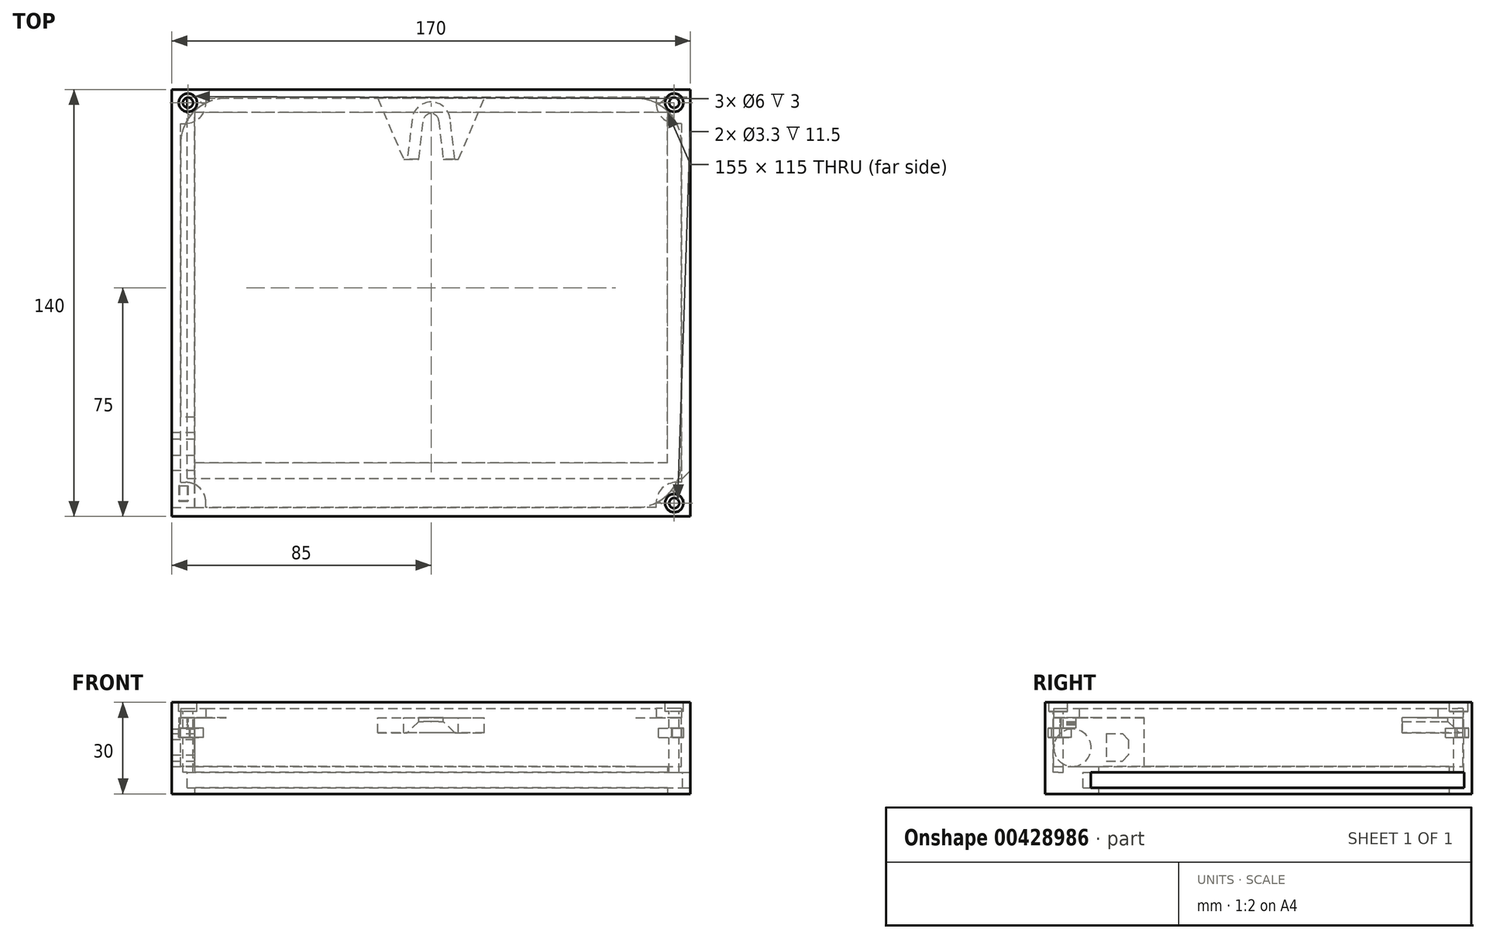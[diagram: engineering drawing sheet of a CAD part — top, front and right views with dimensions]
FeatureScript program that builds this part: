
annotation { "Feature Type Name" : "Feature", "Feature Type Description" : "" }
export const myFeature = defineFeature(function(context is Context, id is Id, definition is map)
    precondition{}
    {
        {
            var Q0;
            Q0=qCreatedBy(makeId("Top.planeOp"),FACE);
            var sketch = newSketch(context, id + "F0", { "sketchPlane" : qUnion([Q0])});
            skLineSegment(sketch, "E0.bottom", {"start": v(0, 0) * mm, "end": v(170, 0) * mm});
            skLineSegment(sketch, "E0.top", {"start": v(0, 140) * mm, "end": v(170, 140) * mm});
            skLineSegment(sketch, "E0.left", {"start": v(0, 0) * mm, "end": v(0, 140) * mm});
            skLineSegment(sketch, "E0.right", {"start": v(170, 0) * mm, "end": v(170, 140) * mm});
            skLineSegment(sketch, "E1.bottom", {"start": v(7.5, 132.5) * mm, "end": v(162.5, 132.5) * mm});
            skLineSegment(sketch, "E1.top", {"start": v(7.5, 17.5) * mm, "end": v(162.5, 17.5) * mm});
            skLineSegment(sketch, "E1.left", {"start": v(7.5, 132.5) * mm, "end": v(7.5, 17.5) * mm});
            skLineSegment(sketch, "E1.right", {"start": v(162.5, 132.5) * mm, "end": v(162.5, 17.5) * mm});
            skSolve(sketch);
        }
        {
            var Q0;
            Q0 = qSketchRegion(id + "F0", true);
            extrude(context, id + "F1", {"entities" : qUnion([Q0]), "depth" : 25 * mm});
        }
        {
            var Q0;
            Q0=makeQuery(id+"F1.opExtrude","SWEPT_FACE",FACE,{"disambiguationData":[OSD([sQuery(id+"F0.wireOp",EDGE,"E0.right")])]});
            var sketch = newSketch(context, id + "F2", { "sketchPlane" : qUnion([Q0])});
            skLineSegment(sketch, "E2.0.0", {"start": v(17.5, 0) * mm, "end": v(132.5, 0) * mm, "construction": true});
            skLineSegment(sketch, "E2.0.1", {"start": v(132.5, 0) * mm, "end": v(132.5, 25) * mm, "construction": true});
            skLineSegment(sketch, "E2.0.2", {"start": v(132.5, 25) * mm, "end": v(17.5, 25) * mm, "construction": true});
            skLineSegment(sketch, "E2.0.3", {"start": v(17.5, 25) * mm, "end": v(17.5, 0) * mm, "construction": true});
            skLineSegment(sketch, "E3.0.3", {"start": v(132.5, 25) * mm, "end": v(132.5, 0) * mm, "construction": true});
            skLineSegment(sketch, "E4.bottom", {"start": v(12.5, 2) * mm, "end": v(137.5, 2) * mm});
            skLineSegment(sketch, "E4.top", {"start": v(12.5, 7) * mm, "end": v(137.5, 7) * mm});
            skLineSegment(sketch, "E4.left", {"start": v(12.5, 2) * mm, "end": v(12.5, 7) * mm});
            skLineSegment(sketch, "E4.right", {"start": v(137.5, 2) * mm, "end": v(137.5, 7) * mm});
            skSolve(sketch);
        }
        {
            var Q0;
            Q0 = qSketchRegion(id + "F2", true);
            extrude(context, id + "F3", {"entities" : qUnion([Q0]), "operationType" : NewBodyOperationType.REMOVE, "oppositeDirection" : true, "depth" : 165 * mm});
        }
        {
            var Q0;
            Q0=makeQuery(id+"F3.boolean.opBoolean","COPY",FACE,{"derivedFrom":makeQuery(id+"F3.opExtrude","SWEPT_FACE",FACE,{"disambiguationData":[OSD([sQuery(id+"F2.wireOp",EDGE,"E4.top")])]})});
            var sketch = newSketch(context, id + "F4", { "sketchPlane" : qUnion([Q0])});
            skLineSegment(sketch, "E5", {"start": v(167.5, -12.5) * mm, "end": v(170, -15) * mm});
            skLineSegment(sketch, "E6", {"start": v(170, -15) * mm, "end": v(170, -12.5) * mm});
            skLineSegment(sketch, "E7", {"start": v(170, -12.5) * mm, "end": v(167.5, -12.5) * mm});
            skSolve(sketch);
        }
        {
            var Q0;
            Q0=makeQuery(id+"F4.imprint","IMPRINT",FACE,{"disambiguationData":[TD([[makeQuery(id+"F4.imprint","IMPRINT",EDGE,{"derivedFrom":sQuery(id+"F4.wireOp",EDGE,"E5")}),1.0]])]});
            extrude(context, id + "F5", {"entities" : qUnion([Q0]), "operationType" : NewBodyOperationType.ADD, "endBound" : BoundingType.UP_TO_NEXT, "depth" : 25 * mm});
        }
        {
            var Q0;
            Q0=makeQuery(id+"F1.opExtrude","CAP_FACE",FACE,{"disambiguationData":[OSD([sQuery(id+"F0.wireOp",EDGE,"E0.bottom"),sQuery(id+"F0.wireOp",EDGE,"E0.top"),sQuery(id+"F0.wireOp",EDGE,"E0.left"),sQuery(id+"F0.wireOp",EDGE,"E0.right"),sQuery(id+"F0.wireOp",EDGE,"E1.bottom"),sQuery(id+"F0.wireOp",EDGE,"E1.top"),sQuery(id+"F0.wireOp",EDGE,"E1.left"),sQuery(id+"F0.wireOp",EDGE,"E1.right")])],"isStart":false});
            var sketch = newSketch(context, id + "F6", { "sketchPlane" : qUnion([Q0])});
            skLineSegment(sketch, "E8.0", {"start": v(167.12, 137.12) * mm, "end": v(2.88, 137.12) * mm});
            skLineSegment(sketch, "E8.1", {"start": v(167.12, 2.88) * mm, "end": v(167.12, 137.12) * mm});
            skLineSegment(sketch, "E8.2", {"start": v(2.88, 2.88) * mm, "end": v(167.12, 2.88) * mm});
            skLineSegment(sketch, "E8.3", {"start": v(2.88, 137.12) * mm, "end": v(2.88, 2.88) * mm});
            skSolve(sketch);
        }
        {
            var Q0;
            Q0 = qSketchRegion(id + "F6", true);
            extrude(context, id + "F7", {"entities" : qUnion([Q0]), "operationType" : NewBodyOperationType.REMOVE, "oppositeDirection" : true, "depth" : 16 * mm});
        }
        {
            var Q0;
            Q0=makeQuery(id+"F7.boolean.opBoolean","COPY",EDGE,{"derivedFrom":makeQuery(id+"F7.opExtrude","SWEPT_EDGE",EDGE,{"disambiguationData":[OSD([sQuery(id+"F6.wireOp",EDGE,"E8.0"),sQuery(id+"F6.wireOp",EDGE,"E8.3")])]})});
            var Q1;
            Q1=makeQuery(id+"F7.boolean.opBoolean","COPY",EDGE,{"derivedFrom":makeQuery(id+"F7.opExtrude","SWEPT_EDGE",EDGE,{"disambiguationData":[OSD([sQuery(id+"F6.wireOp",EDGE,"E8.0"),sQuery(id+"F6.wireOp",EDGE,"E8.1")])]})});
            var Q2;
            Q2=makeQuery(id+"F7.boolean.opBoolean","COPY",EDGE,{"derivedFrom":makeQuery(id+"F7.opExtrude","SWEPT_EDGE",EDGE,{"disambiguationData":[OSD([sQuery(id+"F6.wireOp",EDGE,"E8.1"),sQuery(id+"F6.wireOp",EDGE,"E8.2")])]})});
            fillet(context, id + "F8", {"entities" : qUnion([Q0, Q1, Q2]), "radius" : 15 * mm, "tangentPropagation" : true, "allowEdgeOverflow" : false});
        }
        {
            var Q0;
            Q0=makeQuery(id+"F7.boolean.opBoolean","COPY",FACE,{"derivedFrom":makeQuery(id+"F7.opExtrude","SWEPT_FACE",FACE,{"disambiguationData":[OSD([sQuery(id+"F6.wireOp",EDGE,"E8.3")])]})});
            var sketch = newSketch(context, id + "F9", { "sketchPlane" : qUnion([Q0])});
            skLineSegment(sketch, "E9.0.0", {"start": v(2.88, 9) * mm, "end": v(122.12, 9) * mm, "construction": true});
            skLineSegment(sketch, "E9.0.1", {"start": v(122.12, 9) * mm, "end": v(122.12, 25) * mm, "construction": true});
            skLineSegment(sketch, "E9.0.2", {"start": v(122.12, 25) * mm, "end": v(2.88, 25) * mm, "construction": true});
            skLineSegment(sketch, "E9.0.3", {"start": v(2.88, 25) * mm, "end": v(2.88, 9) * mm, "construction": true});
            skCircle(sketch, "E10", {"center": v(9, 15.13) * mm, "radius": 6.12 * mm});
            skSolve(sketch);
        }
        {
            var Q0;
            {var subQ0=sQuery(id+"F9.wireOp",EDGE,"E10");var subQ1=sQuery(id+"F6.wireOp",EDGE,"E8.3");var subQ3=makeQuery(id+"F9.imprint","INTERSECT",VERTEX,{"derivedFrom":[makeQuery(id+"F7.boolean.opBoolean","COPY",EDGE,{"derivedFrom":makeQuery(id+"F7.opExtrude","CAP_EDGE",EDGE,{"disambiguationData":[OSD([subQ1])],"isStart":false})}),subQ0]});Q0=makeQuery(id+"F9.imprint","IMPRINT",FACE,{"disambiguationData":[TD([[makeQuery(id+"F9.imprint","IMPRINT",EDGE,{"disambiguationData":[TD([[subQ3,1.0]])],"derivedFrom":subQ0}),1.0]])]});}
            extrude(context, id + "F10", {"entities" : qUnion([Q0]), "operationType" : NewBodyOperationType.REMOVE, "endBound" : BoundingType.THROUGH_ALL, "oppositeDirection" : true, "depth" : 25 * mm});
        }
        {
            var Q0;
            {var subQ0=sQuery(id+"F6.wireOp",EDGE,"E8.3");var subQ1=makeQuery(id+"F7.boolean.opBoolean","COPY",FACE,{"derivedFrom":makeQuery(id+"F7.opExtrude","SWEPT_FACE",FACE,{"disambiguationData":[OSD([subQ0])]})});var subQ2=sQuery(id+"F6.wireOp",EDGE,"E8.2");var subQ3=sQuery(id+"F6.wireOp",EDGE,"E8.0");Q0=makeQuery(id+"F10.boolean.opBoolean","SPLIT",FACE,{"disambiguationData":[TD([makeQuery(id+"F1.opExtrude","CAP_FACE",FACE,{"disambiguationData":[OSD([sQuery(id+"F0.wireOp",EDGE,"E0.bottom"),sQuery(id+"F0.wireOp",EDGE,"E0.top"),sQuery(id+"F0.wireOp",EDGE,"E0.left"),sQuery(id+"F0.wireOp",EDGE,"E0.right"),sQuery(id+"F0.wireOp",EDGE,"E1.bottom"),sQuery(id+"F0.wireOp",EDGE,"E1.top"),sQuery(id+"F0.wireOp",EDGE,"E1.left"),sQuery(id+"F0.wireOp",EDGE,"E1.right")])],"isStart":false}),makeQuery(id+"F7.boolean.opBoolean","COPY",FACE,{"derivedFrom":makeQuery(id+"F7.opExtrude","CAP_FACE",FACE,{"disambiguationData":[OSD([subQ3,sQuery(id+"F6.wireOp",EDGE,"E8.1"),subQ2,subQ0])],"isStart":false})}),makeQuery(id+"F7.boolean.opBoolean","COPY",FACE,{"derivedFrom":makeQuery(id+"F7.opExtrude","SWEPT_FACE",FACE,{"disambiguationData":[OSD([subQ2])]})}),subQ1,makeQuery(id+"F8.opFillet","BLEND_FACE",FACE,{"disambiguationData":[OSD([subQ3,subQ0])]}),makeQuery(id+"F10.opExtrude","SWEPT_FACE",FACE,{"disambiguationData":[OSD([sQuery(id+"F9.wireOp",EDGE,"E10")])]})])],"derivedFrom":subQ1});}
            var sketch = newSketch(context, id + "F11", { "sketchPlane" : qUnion([Q0])});
            skArc(sketch, "E11.0", {"start": v(9, 9) * mm, "mid": v(13.34, 19.46) * mm, "end": v(2.88, 15.13) * mm});
            skArc(sketch, "E12.0", {"start": v(2.88, 15.13) * mm, "mid": v(4.67, 10.8) * mm, "end": v(9, 9) * mm});
            skLineSegment(sketch, "E13.bottom", {"start": v(2.88, 9) * mm, "end": v(17.5, 9) * mm});
            skLineSegment(sketch, "E13.top", {"start": v(2.88, 25) * mm, "end": v(17.5, 25) * mm});
            skLineSegment(sketch, "E13.left", {"start": v(2.88, 9) * mm, "end": v(2.88, 25) * mm});
            skLineSegment(sketch, "E13.right", {"start": v(17.5, 9) * mm, "end": v(17.5, 9) * mm});
            skLineSegment(sketch, "E14.0", {"start": v(17.5, 9) * mm, "end": v(17.5, 7) * mm, "construction": true});
            skLineSegment(sketch, "E15", {"start": v(17.5, 9) * mm, "end": v(17.5, 25) * mm});
            skSolve(sketch);
        }
        {
            var Q0;
            Q0 = qSketchRegion(id + "F11", true);
            var Q1;
            {var subQ0=sQuery(id+"F0.wireOp",EDGE,"E1.left");Q1=makeQuery(id+"F3.boolean.opBoolean","SPLIT",FACE,{"disambiguationData":[TD([makeQuery(id+"F3.opExtrude","SWEPT_FACE",FACE,{"disambiguationData":[OSD([sQuery(id+"F2.wireOp",EDGE,"E4.top")])]})])],"derivedFrom":makeQuery(id+"F1.opExtrude","SWEPT_FACE",FACE,{"disambiguationData":[OSD([subQ0])]})});}
            extrude(context, id + "F12", {"entities" : qUnion([Q0]), "operationType" : NewBodyOperationType.ADD, "endBound" : BoundingType.UP_TO_SURFACE, "endBoundEntityFace" : qUnion([Q1]), "depth" : 7.5 * mm});
        }
        {
            var Q0;
            Q0=makeQuery(id+"F12.opExtrude","CAP_FACE",FACE,{"disambiguationData":[OSD([sQuery(id+"F11.wireOp",EDGE,"E13.bottom"),sQuery(id+"F11.wireOp",EDGE,"E13.top"),sQuery(id+"F11.wireOp",EDGE,"E13.left"),sQuery(id+"F11.wireOp",EDGE,"E15")])],"isStart":true});
            extrude(context, id + "F13", {"entities" : qUnion([Q0]), "operationType" : NewBodyOperationType.REMOVE, "endBound" : BoundingType.UP_TO_NEXT, "oppositeDirection" : true, "depth" : 25 * mm});
        }
        {
            var Q0;
            Q0=makeQuery(id+"F12.opExtrude","SWEPT_FACE",FACE,{"disambiguationData":[OSD([sQuery(id+"F11.wireOp",EDGE,"E15")])]});
            extrude(context, id + "F14", {"entities" : qUnion([Q0]), "operationType" : NewBodyOperationType.ADD, "depth" : 15 * mm});
        }
        {
            var Q0;
            {var subQ0=sQuery(id+"F11.wireOp",EDGE,"E15");var subQ1=sQuery(id+"F6.wireOp",EDGE,"E8.2");var subQ2=sQuery(id+"F11.wireOp",EDGE,"E13.top");var subQ3=makeQuery(id+"F12.opExtrude","CAP_FACE",FACE,{"disambiguationData":[OSD([sQuery(id+"F11.wireOp",EDGE,"E13.bottom"),subQ2,sQuery(id+"F11.wireOp",EDGE,"E13.left"),subQ0])],"isStart":false});var subQ4=sQuery(id+"F0.wireOp",EDGE,"E1.left");var subQ5=makeQuery(id+"F1.opExtrude","SWEPT_FACE",FACE,{"disambiguationData":[OSD([subQ4])]});var subQ6=sQuery(id+"F0.wireOp",EDGE,"E1.top");var subQ7=makeQuery(id+"F1.opExtrude","SWEPT_FACE",FACE,{"disambiguationData":[OSD([subQ6])]});var subQ8=sQuery(id+"F0.wireOp",EDGE,"E1.bottom");var subQ9=makeQuery(id+"F1.opExtrude","CAP_FACE",FACE,{"disambiguationData":[OSD([sQuery(id+"F0.wireOp",EDGE,"E0.bottom"),sQuery(id+"F0.wireOp",EDGE,"E0.top"),sQuery(id+"F0.wireOp",EDGE,"E0.left"),sQuery(id+"F0.wireOp",EDGE,"E0.right"),subQ8,subQ6,subQ4,sQuery(id+"F0.wireOp",EDGE,"E1.right")])],"isStart":false});var subQ10=sQuery(id+"F9.wireOp",EDGE,"E10");Q0=makeQuery(id+"F14.boolean.opBoolean","MERGE",FACE,{"derivedFrom":[makeQuery(id+"F3.boolean.opBoolean","SPLIT",FACE,{"disambiguationData":[TD([makeQuery(id+"F3.opExtrude","SWEPT_FACE",FACE,{"disambiguationData":[OSD([sQuery(id+"F2.wireOp",EDGE,"E4.top")])]})])],"derivedFrom":subQ5}),makeQuery(id+"F13.boolean.opBoolean","SPLIT",FACE,{"disambiguationData":[TD([subQ9,subQ7,subQ5,makeQuery(id+"F7.boolean.opBoolean","COPY",FACE,{"derivedFrom":makeQuery(id+"F7.opExtrude","CAP_FACE",FACE,{"disambiguationData":[OSD([sQuery(id+"F6.wireOp",EDGE,"E8.0"),sQuery(id+"F6.wireOp",EDGE,"E8.1"),subQ1,sQuery(id+"F6.wireOp",EDGE,"E8.3")])],"isStart":false})}),makeQuery(id+"F7.boolean.opBoolean","COPY",FACE,{"derivedFrom":makeQuery(id+"F7.opExtrude","SWEPT_FACE",FACE,{"disambiguationData":[OSD([subQ1])]})}),makeQuery(id+"F10.boolean.opBoolean","COPY",FACE,{"derivedFrom":makeQuery(id+"F10.opExtrude","SWEPT_FACE",FACE,{"disambiguationData":[OSD([subQ10])]})}),subQ3,makeQuery(id+"F12.opExtrude","SWEPT_FACE",FACE,{"disambiguationData":[OSD([subQ2])]}),makeQuery(id+"F12.opExtrude","SWEPT_FACE",FACE,{"disambiguationData":[OSD([subQ0])]}),makeQuery(id+"F13.opExtrude","SWEPT_FACE",FACE,{"disambiguationData":[OSD([subQ10])]})])],"derivedFrom":subQ3}),makeQuery(id+"F14.opExtrude","SWEPT_FACE",FACE,{"disambiguationData":[OSD([subQ0]),TDD([makeQuery(id+"F12.opExtrude","CAP_EDGE",EDGE,{"disambiguationData":[OSD([subQ0])],"isStart":false})])]})]});}
            var sketch = newSketch(context, id + "F15", { "sketchPlane" : qUnion([Q0])});
            skLineSegment(sketch, "E16.bottom", {"start": v(20.13, 19.75) * mm, "end": v(27.38, 19.75) * mm});
            skLineSegment(sketch, "E16.top", {"start": v(20.13, 10.75) * mm, "end": v(27.38, 10.75) * mm});
            skLineSegment(sketch, "E16.left", {"start": v(20.13, 19.75) * mm, "end": v(20.13, 10.75) * mm});
            skLineSegment(sketch, "E16.right", {"start": v(27.38, 19.75) * mm, "end": v(27.38, 10.75) * mm});
            skLineSegment(sketch, "E17.0", {"start": v(9, 9) * mm, "end": v(17.5, 9) * mm, "construction": true});
            skSolve(sketch);
        }
        {
            var Q0;
            Q0=makeQuery(id+"F15.imprint","IMPRINT",FACE,{"disambiguationData":[TD([[makeQuery(id+"F15.imprint","IMPRINT",EDGE,{"derivedFrom":sQuery(id+"F15.wireOp",EDGE,"E16.bottom")}),-1.0]])]});
            extrude(context, id + "F16", {"entities" : qUnion([Q0]), "operationType" : NewBodyOperationType.REMOVE, "endBound" : BoundingType.UP_TO_NEXT, "oppositeDirection" : true, "depth" : 25 * mm});
        }
        {
            var Q0;
            Q0=makeQuery(id+"F16.boolean.opBoolean","COPY",EDGE,{"derivedFrom":makeQuery(id+"F16.opExtrude","SWEPT_EDGE",EDGE,{"disambiguationData":[OSD([sQuery(id+"F15.wireOp",EDGE,"E16.top"),sQuery(id+"F15.wireOp",EDGE,"E16.right")])]})});
            var Q1;
            Q1=makeQuery(id+"F16.boolean.opBoolean","COPY",EDGE,{"derivedFrom":makeQuery(id+"F16.opExtrude","SWEPT_EDGE",EDGE,{"disambiguationData":[OSD([sQuery(id+"F15.wireOp",EDGE,"E16.bottom"),sQuery(id+"F15.wireOp",EDGE,"E16.right")])]})});
            chamfer(context, id + "F17", {"entities" : qUnion([Q0, Q1]), "width" : 2 * mm, "tangentPropagation" : true});
        }
        {
            var Q0;
            {var subQ0=sQuery(id+"F11.wireOp",EDGE,"E13.top");Q0=makeQuery(id+"F14.boolean.opBoolean","MERGE",FACE,{"derivedFrom":[makeQuery(id+"F12.boolean.opBoolean","MERGE",FACE,{"derivedFrom":[makeQuery(id+"F1.opExtrude","CAP_FACE",FACE,{"disambiguationData":[OSD([sQuery(id+"F0.wireOp",EDGE,"E0.bottom"),sQuery(id+"F0.wireOp",EDGE,"E0.top"),sQuery(id+"F0.wireOp",EDGE,"E0.left"),sQuery(id+"F0.wireOp",EDGE,"E0.right"),sQuery(id+"F0.wireOp",EDGE,"E1.bottom"),sQuery(id+"F0.wireOp",EDGE,"E1.top"),sQuery(id+"F0.wireOp",EDGE,"E1.left"),sQuery(id+"F0.wireOp",EDGE,"E1.right")])],"isStart":false}),makeQuery(id+"F12.opExtrude","SWEPT_FACE",FACE,{"disambiguationData":[OSD([subQ0])]})]}),makeQuery(id+"F14.opExtrude","SWEPT_FACE",FACE,{"disambiguationData":[OSD([sQuery(id+"F6.wireOp",EDGE,"E8.3"),subQ0,sQuery(id+"F11.wireOp",EDGE,"E15")])]})]});}
            var sketch = newSketch(context, id + "F18", { "sketchPlane" : qUnion([Q0])});
            skLineSegment(sketch, "E18", {"start": v(67.5, 137.12) * mm, "end": v(76, 117.12) * mm});
            skLineSegment(sketch, "E19", {"start": v(76, 117.12) * mm, "end": v(81, 117.12) * mm});
            skLineSegment(sketch, "E20", {"start": v(89, 117.12) * mm, "end": v(87.25, 132.12) * mm});
            skLineSegment(sketch, "E21", {"start": v(82.75, 132.12) * mm, "end": v(87.25, 132.12) * mm});
            skLineSegment(sketch, "E22", {"start": v(82.75, 132.12) * mm, "end": v(81, 117.12) * mm});
            skLineSegment(sketch, "E23", {"start": v(89, 117.12) * mm, "end": v(94, 117.12) * mm});
            skLineSegment(sketch, "E24", {"start": v(94, 117.12) * mm, "end": v(102.5, 137.12) * mm});
            skLineSegment(sketch, "E25", {"start": v(102.5, 137.12) * mm, "end": v(67.5, 137.12) * mm});
            skSolve(sketch);
        }
        {
            var Q0;
            Q0 = qSketchRegion(id + "F18", true);
            extrude(context, id + "F19", {"entities" : qUnion([Q0]), "operationType" : NewBodyOperationType.ADD, "oppositeDirection" : true, "depth" : 5 * mm});
        }
        {
            var Q0;
            Q0=makeQuery(id+"F19.opExtrude","SWEPT_EDGE",EDGE,{"disambiguationData":[OSD([sQuery(id+"F18.wireOp",EDGE,"E21"),sQuery(id+"F18.wireOp",EDGE,"E22")])]});
            var Q1;
            Q1=makeQuery(id+"F19.opExtrude","SWEPT_EDGE",EDGE,{"disambiguationData":[OSD([sQuery(id+"F18.wireOp",EDGE,"E20"),sQuery(id+"F18.wireOp",EDGE,"E21")])]});
            fillet(context, id + "F20", {"entities" : qUnion([Q0, Q1]), "radius" : 2.5 * mm, "tangentPropagation" : true, "allowEdgeOverflow" : false});
        }
        {
            var Q0;
            {var subQ0=sQuery(id+"F18.wireOp",EDGE,"E22");var subQ1=sQuery(id+"F18.wireOp",EDGE,"E21");Q0=makeQuery(id+"F20.opFillet","BLEND_EDGE",EDGE,{"blendedFrom":[makeQuery(id+"F19.opExtrude","SWEPT_EDGE",EDGE,{"disambiguationData":[OSD([subQ1,subQ0])]}),makeQuery(id+"F19.opExtrude","CAP_FACE",FACE,{"disambiguationData":[OSD([sQuery(id+"F18.wireOp",EDGE,"E18"),sQuery(id+"F18.wireOp",EDGE,"E19"),sQuery(id+"F18.wireOp",EDGE,"E20"),subQ1,subQ0,sQuery(id+"F18.wireOp",EDGE,"E23"),sQuery(id+"F18.wireOp",EDGE,"E24"),sQuery(id+"F18.wireOp",EDGE,"E25")])],"isStart":false})],"blendedInto":[makeQuery(id+"F19.opExtrude","CAP_FACE",FACE,{"disambiguationData":[OSD([sQuery(id+"F18.wireOp",EDGE,"E18"),sQuery(id+"F18.wireOp",EDGE,"E19"),sQuery(id+"F18.wireOp",EDGE,"E20"),subQ1,subQ0,sQuery(id+"F18.wireOp",EDGE,"E23"),sQuery(id+"F18.wireOp",EDGE,"E24"),sQuery(id+"F18.wireOp",EDGE,"E25")])],"isStart":false})]});}
            chamfer(context, id + "F21", {"entities" : qUnion([Q0]), "width" : 3.75 * mm, "tangentPropagation" : true});
        }
        {
            var Q0;
            {var subQ0=sQuery(id+"F11.wireOp",EDGE,"E13.top");Q0=makeQuery(id+"F19.boolean.opBoolean","MERGE",FACE,{"derivedFrom":[makeQuery(id+"F14.boolean.opBoolean","MERGE",FACE,{"derivedFrom":[makeQuery(id+"F12.boolean.opBoolean","MERGE",FACE,{"derivedFrom":[makeQuery(id+"F1.opExtrude","CAP_FACE",FACE,{"disambiguationData":[OSD([sQuery(id+"F0.wireOp",EDGE,"E0.bottom"),sQuery(id+"F0.wireOp",EDGE,"E0.top"),sQuery(id+"F0.wireOp",EDGE,"E0.left"),sQuery(id+"F0.wireOp",EDGE,"E0.right"),sQuery(id+"F0.wireOp",EDGE,"E1.bottom"),sQuery(id+"F0.wireOp",EDGE,"E1.top"),sQuery(id+"F0.wireOp",EDGE,"E1.left"),sQuery(id+"F0.wireOp",EDGE,"E1.right")])],"isStart":false}),makeQuery(id+"F12.opExtrude","SWEPT_FACE",FACE,{"disambiguationData":[OSD([subQ0])]})]}),makeQuery(id+"F14.opExtrude","SWEPT_FACE",FACE,{"disambiguationData":[OSD([sQuery(id+"F6.wireOp",EDGE,"E8.3"),subQ0,sQuery(id+"F11.wireOp",EDGE,"E15")])]})]}),makeQuery(id+"F19.opExtrude","CAP_FACE",FACE,{"disambiguationData":[OSD([sQuery(id+"F18.wireOp",EDGE,"E18"),sQuery(id+"F18.wireOp",EDGE,"E19"),sQuery(id+"F18.wireOp",EDGE,"E20"),sQuery(id+"F18.wireOp",EDGE,"E21"),sQuery(id+"F18.wireOp",EDGE,"E22"),sQuery(id+"F18.wireOp",EDGE,"E23"),sQuery(id+"F18.wireOp",EDGE,"E24"),sQuery(id+"F18.wireOp",EDGE,"E25")])],"isStart":true})]});}
            cPlane(context, id + "F22", {"entities" : qUnion([Q0]), "cplaneType" : CPlaneType.OFFSET, "offset" : 5 * mm, "oppositeDirection" : true, "width" : 150 * mm, "height" : 150 * mm});
        }
        {
            var Q0;
            Q0=qCreatedBy(id+"F22.planeOp",FACE);
            var sketch = newSketch(context, id + "F23", { "sketchPlane" : qUnion([Q0])});
            skLineSegment(sketch, "E26.0.0", {"start": v(170, 140) * mm, "end": v(0, 140) * mm, "construction": true});
            skLineSegment(sketch, "E26.0.1", {"start": v(0, 140) * mm, "end": v(0, 0) * mm, "construction": true});
            skLineSegment(sketch, "E26.0.2", {"start": v(0, 0) * mm, "end": v(170, 0) * mm, "construction": true});
            skLineSegment(sketch, "E26.0.3", {"start": v(170, 0) * mm, "end": v(170, 140) * mm, "construction": true});
            skLineSegment(sketch, "E27", {"start": v(0, 140) * mm, "end": v(170, 0) * mm, "construction": true});
            skLineSegment(sketch, "E28", {"start": v(0, 0) * mm, "end": v(170, 140) * mm, "construction": true});
            skCircle(sketch, "E29.cCircle", {"center": v(5.27, 135.66) * mm, "radius": 2.85 * mm, "construction": true});
            skLineSegment(sketch, "E29.0", {"start": v(5.81, 138.9) * mm, "end": v(8.35, 136.81) * mm});
            skLineSegment(sketch, "E29.1", {"start": v(8.35, 136.81) * mm, "end": v(7.81, 133.57) * mm, "construction": true});
            skLineSegment(sketch, "E29.2", {"start": v(7.81, 133.57) * mm, "end": v(4.73, 132.41) * mm, "construction": true});
            skLineSegment(sketch, "E29.3", {"start": v(4.73, 132.41) * mm, "end": v(2.2, 134.5) * mm});
            skLineSegment(sketch, "E29.4", {"start": v(2.2, 134.5) * mm, "end": v(2.73, 137.75) * mm});
            skLineSegment(sketch, "E29.5", {"start": v(2.73, 137.75) * mm, "end": v(5.81, 138.9) * mm});
            skPoint(sketch, "E29.0.midPoint", {"position": v(7.08, 137.86) * mm});
            skCircle(sketch, "E30.cCircle", {"center": v(164.73, 135.66) * mm, "radius": 2.85 * mm, "construction": true});
            skLineSegment(sketch, "E30.0", {"start": v(161.65, 136.81) * mm, "end": v(164.19, 138.9) * mm});
            skLineSegment(sketch, "E30.1", {"start": v(164.19, 138.9) * mm, "end": v(167.27, 137.75) * mm});
            skLineSegment(sketch, "E30.2", {"start": v(167.27, 137.75) * mm, "end": v(167.8, 134.5) * mm});
            skLineSegment(sketch, "E30.3", {"start": v(167.8, 134.5) * mm, "end": v(165.27, 132.41) * mm});
            skLineSegment(sketch, "E30.4", {"start": v(165.27, 132.41) * mm, "end": v(162.19, 133.57) * mm, "construction": true});
            skLineSegment(sketch, "E30.5", {"start": v(162.19, 133.57) * mm, "end": v(161.65, 136.81) * mm, "construction": true});
            skPoint(sketch, "E30.0.midPoint", {"position": v(162.92, 137.86) * mm});
            skCircle(sketch, "E31.cCircle", {"center": v(164.73, 4.34) * mm, "radius": 2.85 * mm, "construction": true});
            skLineSegment(sketch, "E31.0", {"start": v(165.27, 7.59) * mm, "end": v(167.8, 5.5) * mm});
            skLineSegment(sketch, "E31.1", {"start": v(167.8, 5.5) * mm, "end": v(167.27, 2.25) * mm});
            skLineSegment(sketch, "E31.2", {"start": v(167.27, 2.25) * mm, "end": v(164.19, 1.1) * mm});
            skLineSegment(sketch, "E31.3", {"start": v(164.19, 1.1) * mm, "end": v(161.65, 3.19) * mm});
            skLineSegment(sketch, "E31.4", {"start": v(161.65, 3.19) * mm, "end": v(162.19, 6.43) * mm, "construction": true});
            skLineSegment(sketch, "E31.5", {"start": v(162.19, 6.43) * mm, "end": v(165.27, 7.59) * mm, "construction": true});
            skPoint(sketch, "E31.0.midPoint", {"position": v(166.54, 6.54) * mm});
            skArc(sketch, "E32.0", {"start": v(6.04, 131.33) * mm, "mid": v(8.04, 133.44) * mm, "end": v(10.4, 135.12) * mm});
            skArc(sketch, "E33.0", {"start": v(159.6, 135.12) * mm, "mid": v(161.96, 133.44) * mm, "end": v(163.96, 131.33) * mm});
            skArc(sketch, "E34.0", {"start": v(163.96, 8.67) * mm, "mid": v(161.96, 6.56) * mm, "end": v(159.6, 4.88) * mm});
            skLineSegment(sketch, "E35", {"start": v(4.73, 132.41) * mm, "end": v(6.04, 131.33) * mm});
            skLineSegment(sketch, "E36", {"start": v(8.35, 136.81) * mm, "end": v(10.4, 135.12) * mm});
            skLineSegment(sketch, "E37", {"start": v(165.27, 132.41) * mm, "end": v(163.96, 131.33) * mm});
            skLineSegment(sketch, "E38", {"start": v(161.65, 136.81) * mm, "end": v(159.6, 135.12) * mm});
            skLineSegment(sketch, "E39", {"start": v(165.27, 7.59) * mm, "end": v(163.96, 8.67) * mm});
            skLineSegment(sketch, "E40", {"start": v(161.65, 3.19) * mm, "end": v(159.6, 4.88) * mm});
            skPoint(sketch, "E41.orphan", {"position": v(152.12, 2.88) * mm});
            skPoint(sketch, "E42.orphan", {"position": v(167.12, 17.88) * mm});
            skPoint(sketch, "E43.orphan", {"position": v(167.12, 122.12) * mm});
            skPoint(sketch, "E44.orphan", {"position": v(152.12, 137.12) * mm});
            skPoint(sketch, "E45.orphan", {"position": v(17.88, 137.12) * mm});
            skPoint(sketch, "E46.orphan", {"position": v(2.88, 122.12) * mm});
            skSolve(sketch);
        }
        {
            var Q0;
            Q0 = qSketchRegion(id + "F23", true);
            extrude(context, id + "F24", {"entities" : qUnion([Q0]), "operationType" : NewBodyOperationType.REMOVE, "endBound" : BoundingType.SYMMETRIC, "oppositeDirection" : true, "depth" : 3 * mm});
        }
        {
            var Q0;
            {var subQ0=sQuery(id+"F11.wireOp",EDGE,"E13.top");Q0=makeQuery(id+"F19.boolean.opBoolean","MERGE",FACE,{"derivedFrom":[makeQuery(id+"F14.boolean.opBoolean","MERGE",FACE,{"derivedFrom":[makeQuery(id+"F12.boolean.opBoolean","MERGE",FACE,{"derivedFrom":[makeQuery(id+"F1.opExtrude","CAP_FACE",FACE,{"disambiguationData":[OSD([sQuery(id+"F0.wireOp",EDGE,"E0.bottom"),sQuery(id+"F0.wireOp",EDGE,"E0.top"),sQuery(id+"F0.wireOp",EDGE,"E0.left"),sQuery(id+"F0.wireOp",EDGE,"E0.right"),sQuery(id+"F0.wireOp",EDGE,"E1.bottom"),sQuery(id+"F0.wireOp",EDGE,"E1.top"),sQuery(id+"F0.wireOp",EDGE,"E1.left"),sQuery(id+"F0.wireOp",EDGE,"E1.right")])],"isStart":false}),makeQuery(id+"F12.opExtrude","SWEPT_FACE",FACE,{"disambiguationData":[OSD([subQ0])]})]}),makeQuery(id+"F14.opExtrude","SWEPT_FACE",FACE,{"disambiguationData":[OSD([sQuery(id+"F6.wireOp",EDGE,"E8.3"),subQ0,sQuery(id+"F11.wireOp",EDGE,"E15")])]})]}),makeQuery(id+"F19.opExtrude","CAP_FACE",FACE,{"disambiguationData":[OSD([sQuery(id+"F18.wireOp",EDGE,"E18"),sQuery(id+"F18.wireOp",EDGE,"E19"),sQuery(id+"F18.wireOp",EDGE,"E20"),sQuery(id+"F18.wireOp",EDGE,"E21"),sQuery(id+"F18.wireOp",EDGE,"E22"),sQuery(id+"F18.wireOp",EDGE,"E23"),sQuery(id+"F18.wireOp",EDGE,"E24"),sQuery(id+"F18.wireOp",EDGE,"E25")])],"isStart":true})]});}
            var sketch = newSketch(context, id + "F25", { "sketchPlane" : qUnion([Q0])});
            skLineSegment(sketch, "E47.0.0", {"start": v(2.2, 134.5) * mm, "end": v(6.04, 131.33) * mm, "construction": true});
            skArc(sketch, "E47.0.1", {"start": v(6.04, 131.33) * mm, "mid": v(8.04, 133.44) * mm, "end": v(10.4, 135.12) * mm, "construction": true});
            skLineSegment(sketch, "E47.0.2", {"start": v(10.4, 135.12) * mm, "end": v(5.81, 138.9) * mm, "construction": true});
            skLineSegment(sketch, "E47.0.3", {"start": v(5.81, 138.9) * mm, "end": v(2.73, 137.75) * mm, "construction": true});
            skLineSegment(sketch, "E47.0.4", {"start": v(2.73, 137.75) * mm, "end": v(2.2, 134.5) * mm, "construction": true});
            skLineSegment(sketch, "E48.0.0", {"start": v(164.19, 138.9) * mm, "end": v(159.6, 135.12) * mm, "construction": true});
            skArc(sketch, "E48.0.1", {"start": v(159.6, 135.12) * mm, "mid": v(161.96, 133.44) * mm, "end": v(163.96, 131.33) * mm, "construction": true});
            skLineSegment(sketch, "E48.0.2", {"start": v(163.96, 131.33) * mm, "end": v(167.8, 134.5) * mm, "construction": true});
            skLineSegment(sketch, "E48.0.3", {"start": v(167.8, 134.5) * mm, "end": v(167.27, 137.75) * mm, "construction": true});
            skLineSegment(sketch, "E48.0.4", {"start": v(167.27, 137.75) * mm, "end": v(164.19, 138.9) * mm, "construction": true});
            skLineSegment(sketch, "E49.0.0", {"start": v(167.8, 5.5) * mm, "end": v(163.96, 8.67) * mm, "construction": true});
            skArc(sketch, "E49.0.1", {"start": v(163.96, 8.67) * mm, "mid": v(161.96, 6.56) * mm, "end": v(159.6, 4.88) * mm, "construction": true});
            skLineSegment(sketch, "E49.0.2", {"start": v(159.6, 4.88) * mm, "end": v(164.19, 1.1) * mm, "construction": true});
            skLineSegment(sketch, "E49.0.3", {"start": v(164.19, 1.1) * mm, "end": v(167.27, 2.25) * mm, "construction": true});
            skLineSegment(sketch, "E49.0.4", {"start": v(167.27, 2.25) * mm, "end": v(167.8, 5.5) * mm, "construction": true});
            skLineSegment(sketch, "E50", {"start": v(2.46, 136.13) * mm, "end": v(5.27, 135.66) * mm, "construction": true});
            skLineSegment(sketch, "E51", {"start": v(4.27, 138.33) * mm, "end": v(5.27, 135.66) * mm, "construction": true});
            skCircle(sketch, "E52", {"center": v(5.27, 135.66) * mm, "radius": 1.65 * mm});
            skLineSegment(sketch, "E53", {"start": v(165.73, 138.33) * mm, "end": v(164.73, 135.66) * mm, "construction": true});
            skLineSegment(sketch, "E54", {"start": v(167.54, 136.13) * mm, "end": v(164.73, 135.66) * mm, "construction": true});
            skCircle(sketch, "E55", {"center": v(164.73, 135.66) * mm, "radius": 1.65 * mm});
            skLineSegment(sketch, "E56", {"start": v(165.73, 1.67) * mm, "end": v(164.73, 4.34) * mm, "construction": true});
            skLineSegment(sketch, "E57", {"start": v(164.73, 4.34) * mm, "end": v(167.54, 3.87) * mm, "construction": true});
            skCircle(sketch, "E58", {"center": v(164.73, 4.34) * mm, "radius": 1.65 * mm});
            skSolve(sketch);
        }
        {
            var Q0;
            Q0 = qSketchRegion(id + "F25", true);
            var Q1;
            Q1=makeQuery(id+"F3.boolean.opBoolean","COPY",FACE,{"derivedFrom":makeQuery(id+"F3.opExtrude","SWEPT_FACE",FACE,{"disambiguationData":[OSD([sQuery(id+"F2.wireOp",EDGE,"E4.top")])]})});
            extrude(context, id + "F26", {"entities" : qUnion([Q0]), "operationType" : NewBodyOperationType.REMOVE, "endBound" : BoundingType.UP_TO_SURFACE, "oppositeDirection" : true, "endBoundEntityFace" : qUnion([Q1]), "depth" : 20 * mm});
        }
        {
            var Q0;
            {var subQ0=sQuery(id+"F11.wireOp",EDGE,"E13.top");Q0=makeQuery(id+"F19.boolean.opBoolean","MERGE",FACE,{"derivedFrom":[makeQuery(id+"F14.boolean.opBoolean","MERGE",FACE,{"derivedFrom":[makeQuery(id+"F12.boolean.opBoolean","MERGE",FACE,{"derivedFrom":[makeQuery(id+"F1.opExtrude","CAP_FACE",FACE,{"disambiguationData":[OSD([sQuery(id+"F0.wireOp",EDGE,"E0.bottom"),sQuery(id+"F0.wireOp",EDGE,"E0.top"),sQuery(id+"F0.wireOp",EDGE,"E0.left"),sQuery(id+"F0.wireOp",EDGE,"E0.right"),sQuery(id+"F0.wireOp",EDGE,"E1.bottom"),sQuery(id+"F0.wireOp",EDGE,"E1.top"),sQuery(id+"F0.wireOp",EDGE,"E1.left"),sQuery(id+"F0.wireOp",EDGE,"E1.right")])],"isStart":false}),makeQuery(id+"F12.opExtrude","SWEPT_FACE",FACE,{"disambiguationData":[OSD([subQ0])]})]}),makeQuery(id+"F14.opExtrude","SWEPT_FACE",FACE,{"disambiguationData":[OSD([sQuery(id+"F6.wireOp",EDGE,"E8.3"),subQ0,sQuery(id+"F11.wireOp",EDGE,"E15")])]})]}),makeQuery(id+"F19.opExtrude","CAP_FACE",FACE,{"disambiguationData":[OSD([sQuery(id+"F18.wireOp",EDGE,"E18"),sQuery(id+"F18.wireOp",EDGE,"E19"),sQuery(id+"F18.wireOp",EDGE,"E20"),sQuery(id+"F18.wireOp",EDGE,"E21"),sQuery(id+"F18.wireOp",EDGE,"E22"),sQuery(id+"F18.wireOp",EDGE,"E23"),sQuery(id+"F18.wireOp",EDGE,"E24"),sQuery(id+"F18.wireOp",EDGE,"E25")])],"isStart":true})]});}
            var sketch = newSketch(context, id + "F27", { "sketchPlane" : qUnion([Q0])});
            skLineSegment(sketch, "E59.0.0", {"start": v(170, 140) * mm, "end": v(0, 140) * mm});
            skLineSegment(sketch, "E59.0.1", {"start": v(0, 140) * mm, "end": v(0, 0) * mm});
            skLineSegment(sketch, "E59.0.2", {"start": v(0, 0) * mm, "end": v(170, 0) * mm});
            skLineSegment(sketch, "E59.0.3", {"start": v(170, 0) * mm, "end": v(170, 140) * mm});
            skCircle(sketch, "E60.0", {"center": v(5.27, 135.66) * mm, "radius": 1.65 * mm});
            skCircle(sketch, "E61.0", {"center": v(164.73, 135.66) * mm, "radius": 1.65 * mm});
            skCircle(sketch, "E62.0", {"center": v(164.73, 4.34) * mm, "radius": 1.65 * mm});
            skSolve(sketch);
        }
        {
            var Q0;
            Q0 = qSketchRegion(id + "F27", true);
            extrude(context, id + "F28", {"entities" : qUnion([Q0]), "depth" : 5 * mm});
        }
        {
            var Q0;
            Q0=makeQuery(id+"F28.opExtrude","CAP_FACE",FACE,{"disambiguationData":[OSD([sQuery(id+"F27.wireOp",EDGE,"E59.0.0"),sQuery(id+"F27.wireOp",EDGE,"E59.0.1"),sQuery(id+"F27.wireOp",EDGE,"E59.0.2"),sQuery(id+"F27.wireOp",EDGE,"E59.0.3"),sQuery(id+"F27.wireOp",EDGE,"E60.0"),sQuery(id+"F27.wireOp",EDGE,"E61.0"),sQuery(id+"F27.wireOp",EDGE,"E62.0")])],"isStart":false});
            var sketch = newSketch(context, id + "F29", { "sketchPlane" : qUnion([Q0])});
            skCircle(sketch, "E63.0", {"center": v(5.27, 135.66) * mm, "radius": 1.65 * mm, "construction": true});
            skCircle(sketch, "E64.0", {"center": v(164.73, 135.66) * mm, "radius": 1.65 * mm, "construction": true});
            skCircle(sketch, "E65.0", {"center": v(164.73, 4.34) * mm, "radius": 1.65 * mm, "construction": true});
            skCircle(sketch, "E66", {"center": v(164.73, 4.34) * mm, "radius": 3 * mm});
            skCircle(sketch, "E67", {"center": v(164.73, 135.66) * mm, "radius": 3 * mm});
            skCircle(sketch, "E68", {"center": v(5.27, 135.66) * mm, "radius": 3 * mm});
            skSolve(sketch);
        }
        {
            var Q0;
            Q0 = qSketchRegion(id + "F29", true);
            extrude(context, id + "F30", {"entities" : qUnion([Q0]), "operationType" : NewBodyOperationType.REMOVE, "oppositeDirection" : true, "depth" : 3 * mm});
        }
        {
            var Q0;
            Q0=makeQuery(id+"F1.opExtrude","SWEPT_FACE",FACE,{"disambiguationData":[OSD([sQuery(id+"F0.wireOp",EDGE,"E0.bottom")])]});
            cPlane(context, id + "F31", {"entities" : qUnion([Q0]), "cplaneType" : CPlaneType.OFFSET, "offset" : 5 * mm, "oppositeDirection" : true, "width" : 150 * mm, "height" : 150 * mm});
        }
        {
            var Q0;
            Q0=qCreatedBy(id+"F31.planeOp",FACE);
            cPlane(context, id + "F32", {"entities" : qUnion([Q0]), "cplaneType" : CPlaneType.OFFSET, "offset" : .25 * mm, "oppositeDirection" : true, "width" : 150 * mm, "height" : 150 * mm});
        }
        {
            var Q0;
            Q0=qCreatedBy(id+"F31.planeOp",FACE);
            var sketch = newSketch(context, id + "F33", { "sketchPlane" : qUnion([Q0])});
            skLineSegment(sketch, "E69.0.0", {"start": v(170, 25) * mm, "end": v(7.5, 25) * mm, "construction": true});
            skLineSegment(sketch, "E70.0.0", {"start": v(7.5, 7) * mm, "end": v(7.5, 9) * mm, "construction": true});
            skLineSegment(sketch, "E70.0.2", {"start": v(7.5, 9) * mm, "end": v(7.5, 25) * mm, "construction": true});
            skLineSegment(sketch, "E70.0.4", {"start": v(7.5, 25) * mm, "end": v(7.5, 15.13) * mm, "construction": true});
            skLineSegment(sketch, "E70.0.5", {"start": v(7.5, 9) * mm, "end": v(7.5, 21.25) * mm, "construction": true});
            skLineSegment(sketch, "E70.0.7", {"start": v(7.5, 9) * mm, "end": v(7.5, 7) * mm, "construction": true});
            skLineSegment(sketch, "E71.0.1", {"start": v(0, 0) * mm, "end": v(0, 25) * mm, "construction": true});
            skLineSegment(sketch, "E71.0.3", {"start": v(0, 25) * mm, "end": v(0, 0) * mm, "construction": true});
            skLineSegment(sketch, "E72.trimOffspring", {"start": v(5, 25) * mm, "end": v(170, 25) * mm, "construction": true});
            skLineSegment(sketch, "E73", {"start": v(0, 25) * mm, "end": v(7.5, 25) * mm, "construction": true});
            skLineSegment(sketch, "E74", {"start": v(3.75, 25) * mm, "end": v(3.75, 21.5) * mm, "construction": true});
            skLineSegment(sketch, "E75", {"start": v(2.25, 25) * mm, "end": v(3.75, 25) * mm});
            skLineSegment(sketch, "E76", {"start": v(2.25, 25) * mm, "end": v(2.25, 23.6) * mm});
            skLineSegment(sketch, "E77", {"start": v(2.25, 23.6) * mm, "end": v(2.5, 23.35) * mm});
            skLineSegment(sketch, "E78", {"start": v(2.5, 23.35) * mm, "end": v(2.5, 22.85) * mm});
            skLineSegment(sketch, "E79", {"start": v(2.5, 22.85) * mm, "end": v(2.25, 22.6) * mm});
            skLineSegment(sketch, "E80", {"start": v(2.25, 22.6) * mm, "end": v(2.25, 21.5) * mm});
            skLineSegment(sketch, "E81", {"start": v(2.25, 21.5) * mm, "end": v(3.75, 21.5) * mm});
            skLineSegment(sketch, "E82.MirrorCS", {"start": v(7.5, 25) * mm, "end": v(0, 25) * mm, "construction": true});
            skLineSegment(sketch, "E83.MirrorCS", {"start": v(5.25, 25) * mm, "end": v(5.25, 23.6) * mm});
            skLineSegment(sketch, "E84.MirrorCS", {"start": v(5.25, 23.6) * mm, "end": v(5, 23.35) * mm});
            skLineSegment(sketch, "E85.MirrorCS", {"start": v(5, 23.35) * mm, "end": v(5, 22.85) * mm});
            skLineSegment(sketch, "E86.MirrorCS", {"start": v(5.25, 22.6) * mm, "end": v(5.25, 21.5) * mm});
            skLineSegment(sketch, "E87.MirrorCS", {"start": v(5.25, 21.5) * mm, "end": v(3.75, 21.5) * mm});
            skLineSegment(sketch, "E88.MirrorCS", {"start": v(5, 22.85) * mm, "end": v(5.25, 22.6) * mm});
            skLineSegment(sketch, "E89", {"start": v(3.75, 25) * mm, "end": v(5.25, 25) * mm});
            skSolve(sketch);
        }
        {
            var Q0;
            Q0 = qSketchRegion(id + "F33", true);
            extrude(context, id + "F34", {"entities" : qUnion([Q0]), "operationType" : NewBodyOperationType.REMOVE, "oppositeDirection" : true, "depth" : 5 * mm});
        }
        {
            var Q0;
            Q0=qCreatedBy(id+"F32.planeOp",FACE);
            var sketch = newSketch(context, id + "F35", { "sketchPlane" : qUnion([Q0])});
            skLineSegment(sketch, "E90.0", {"start": v(2.25, 25) * mm, "end": v(2.25, 23.6) * mm, "construction": true});
            skPoint(sketch, "E91.0", {"position": v(2.37, 23.48) * mm});
            skLineSegment(sketch, "E92.0", {"start": v(2.25, 23.6) * mm, "end": v(2.5, 23.35) * mm, "construction": true});
            skLineSegment(sketch, "E93.0", {"start": v(2.5, 23.35) * mm, "end": v(2.5, 22.85) * mm, "construction": true});
            skLineSegment(sketch, "E94.0", {"start": v(2.5, 22.85) * mm, "end": v(2.25, 22.6) * mm, "construction": true});
            skLineSegment(sketch, "E95.0", {"start": v(2.25, 22.6) * mm, "end": v(2.25, 21.5) * mm, "construction": true});
            skLineSegment(sketch, "E96.0", {"start": v(2.25, 21.5) * mm, "end": v(5.25, 21.5) * mm, "construction": true});
            skLineSegment(sketch, "E97.0", {"start": v(5.25, 22.6) * mm, "end": v(5.25, 21.5) * mm, "construction": true});
            skLineSegment(sketch, "E98.0", {"start": v(5, 22.85) * mm, "end": v(5.25, 22.6) * mm, "construction": true});
            skLineSegment(sketch, "E99.0", {"start": v(5, 23.35) * mm, "end": v(5, 22.85) * mm, "construction": true});
            skLineSegment(sketch, "E100.0", {"start": v(5.25, 23.6) * mm, "end": v(5, 23.35) * mm, "construction": true});
            skLineSegment(sketch, "E101.0", {"start": v(5.25, 25) * mm, "end": v(5.25, 23.6) * mm, "construction": true});
            skLineSegment(sketch, "E102.0", {"start": v(2.25, 25) * mm, "end": v(5.25, 25) * mm, "construction": true});
            skLineSegment(sketch, "E103", {"start": v(2.5, 25) * mm, "end": v(2.5, 22.5) * mm});
            skLineSegment(sketch, "E104", {"start": v(2.5, 25) * mm, "end": v(5, 25) * mm});
            skLineSegment(sketch, "E105", {"start": v(5, 25) * mm, "end": v(5, 22.5) * mm});
            skLineSegment(sketch, "E106", {"start": v(2.5, 22.5) * mm, "end": v(2.35, 22.5) * mm});
            skLineSegment(sketch, "E107", {"start": v(2.35, 22.5) * mm, "end": v(2.35, 21.6) * mm});
            skLineSegment(sketch, "E108", {"start": v(2.35, 21.6) * mm, "end": v(5.15, 21.6) * mm});
            skLineSegment(sketch, "E109", {"start": v(5.15, 21.6) * mm, "end": v(5.15, 22.5) * mm});
            skLineSegment(sketch, "E110", {"start": v(5.15, 22.5) * mm, "end": v(5, 22.5) * mm});
            skSolve(sketch);
        }
        {
            var Q0;
            Q0 = qSketchRegion(id + "F35", true);
            extrude(context, id + "F36", {"entities" : qUnion([Q0]), "operationType" : NewBodyOperationType.ADD, "depth" : 4.5 * mm});
        }
        {
            var Q0;
            Q0=makeQuery(id+"F36.opExtrude","SWEPT_EDGE",EDGE,{"disambiguationData":[OSD([sQuery(id+"F35.wireOp",EDGE,"E106"),sQuery(id+"F35.wireOp",EDGE,"E107")])]});
            var Q1;
            Q1=makeQuery(id+"F36.opExtrude","SWEPT_EDGE",EDGE,{"disambiguationData":[OSD([sQuery(id+"F35.wireOp",EDGE,"E109"),sQuery(id+"F35.wireOp",EDGE,"E110")])]});
            fillet(context, id + "F37", {"entities" : qUnion([Q0, Q1]), "radius" : .1 * mm, "tangentPropagation" : true, "allowEdgeOverflow" : false});
        }
        {
            var Q0;
            Q0=makeQuery(id+"F36.opExtrude","SWEPT_EDGE",EDGE,{"disambiguationData":[OSD([sQuery(id+"F35.wireOp",EDGE,"E107"),sQuery(id+"F35.wireOp",EDGE,"E108")])]});
            var Q1;
            Q1=makeQuery(id+"F36.opExtrude","SWEPT_EDGE",EDGE,{"disambiguationData":[OSD([sQuery(id+"F35.wireOp",EDGE,"E108"),sQuery(id+"F35.wireOp",EDGE,"E109")])]});
            fillet(context, id + "F38", {"entities" : qUnion([Q0, Q1]), "radius" : .5 * mm, "tangentPropagation" : true, "allowEdgeOverflow" : false});
        }
        {
            var Q0;
            Q0=makeQuery(id+"F28.opExtrude","CAP_FACE",FACE,{"disambiguationData":[OSD([sQuery(id+"F27.wireOp",EDGE,"E59.0.0"),sQuery(id+"F27.wireOp",EDGE,"E59.0.1"),sQuery(id+"F27.wireOp",EDGE,"E59.0.2"),sQuery(id+"F27.wireOp",EDGE,"E59.0.3"),sQuery(id+"F27.wireOp",EDGE,"E60.0"),sQuery(id+"F27.wireOp",EDGE,"E61.0"),sQuery(id+"F27.wireOp",EDGE,"E62.0")])],"isStart":true});
            var sketch = newSketch(context, id + "F39", { "sketchPlane" : qUnion([Q0])});
            skLineSegment(sketch, "E111.0", {"start": v(11.15, -137.12) * mm, "end": v(158.85, -137.12) * mm});
            skLineSegment(sketch, "E111.1", {"start": v(2.88, -11.15) * mm, "end": v(2.88, -128.85) * mm});
            skLineSegment(sketch, "E111.2", {"start": v(158.85, -2.88) * mm, "end": v(11.15, -2.88) * mm});
            skLineSegment(sketch, "E111.3", {"start": v(167.12, -128.85) * mm, "end": v(167.12, -11.15) * mm});
            skLineSegment(sketch, "E112.bottom", {"start": v(0, -140) * mm, "end": v(11.15, -140) * mm});
            skLineSegment(sketch, "E112.top", {"start": v(2.88, -128.85) * mm, "end": v(11.15, -128.85) * mm});
            skLineSegment(sketch, "E112.left", {"start": v(0, -140) * mm, "end": v(0, -128.85) * mm});
            skLineSegment(sketch, "E112.right", {"start": v(11.15, -137.12) * mm, "end": v(11.15, -128.85) * mm});
            skLineSegment(sketch, "E113.bottom", {"start": v(170, -140) * mm, "end": v(158.85, -140) * mm});
            skLineSegment(sketch, "E113.top", {"start": v(167.12, -128.85) * mm, "end": v(158.85, -128.85) * mm});
            skLineSegment(sketch, "E113.left", {"start": v(170, -140) * mm, "end": v(170, -128.85) * mm});
            skLineSegment(sketch, "E113.right", {"start": v(158.85, -137.12) * mm, "end": v(158.85, -128.85) * mm});
            skLineSegment(sketch, "E114.bottom", {"start": v(170, 0) * mm, "end": v(158.85, 0) * mm});
            skLineSegment(sketch, "E114.top", {"start": v(167.12, -11.15) * mm, "end": v(158.85, -11.15) * mm});
            skLineSegment(sketch, "E114.left", {"start": v(170, 0) * mm, "end": v(170, -11.15) * mm});
            skLineSegment(sketch, "E114.right", {"start": v(158.85, -2.88) * mm, "end": v(158.85, -11.15) * mm});
            skLineSegment(sketch, "E115.bottom", {"start": v(0, 0) * mm, "end": v(11.15, 0) * mm});
            skLineSegment(sketch, "E115.top", {"start": v(2.88, -11.15) * mm, "end": v(11.15, -11.15) * mm});
            skLineSegment(sketch, "E115.left", {"start": v(0, 0) * mm, "end": v(0, -11.15) * mm});
            skLineSegment(sketch, "E115.right", {"start": v(11.15, -2.88) * mm, "end": v(11.15, -11.15) * mm});
            skSolve(sketch);
        }
        {
            var Q0;
            Q0 = qSketchRegion(id + "F39", true);
            extrude(context, id + "F40", {"entities" : qUnion([Q0]), "operationType" : NewBodyOperationType.REMOVE, "oppositeDirection" : true, "depth" : 3 * mm});
        }
        {
            var Q0;
            Q0=makeQuery(id+"F40.boolean.opBoolean","COPY",EDGE,{"derivedFrom":makeQuery(id+"F40.opExtrude","SWEPT_EDGE",EDGE,{"disambiguationData":[OSD([sQuery(id+"F39.wireOp",EDGE,"E115.top"),sQuery(id+"F39.wireOp",EDGE,"E115.right")])]})});
            var Q1;
            Q1=makeQuery(id+"F40.boolean.opBoolean","COPY",EDGE,{"derivedFrom":makeQuery(id+"F40.opExtrude","SWEPT_EDGE",EDGE,{"disambiguationData":[OSD([sQuery(id+"F39.wireOp",EDGE,"E112.top"),sQuery(id+"F39.wireOp",EDGE,"E112.right")])]})});
            var Q2;
            Q2=makeQuery(id+"F40.boolean.opBoolean","COPY",EDGE,{"derivedFrom":makeQuery(id+"F40.opExtrude","SWEPT_EDGE",EDGE,{"disambiguationData":[OSD([sQuery(id+"F39.wireOp",EDGE,"E113.top"),sQuery(id+"F39.wireOp",EDGE,"E113.right")])]})});
            var Q3;
            Q3=makeQuery(id+"F40.boolean.opBoolean","COPY",EDGE,{"derivedFrom":makeQuery(id+"F40.opExtrude","SWEPT_EDGE",EDGE,{"disambiguationData":[OSD([sQuery(id+"F39.wireOp",EDGE,"E114.top"),sQuery(id+"F39.wireOp",EDGE,"E114.right")])]})});
            fillet(context, id + "F41", {"entities" : qUnion([Q0, Q1, Q2, Q3]), "radius" : 6.6 * mm, "tangentPropagation" : true, "allowEdgeOverflow" : false});
        }
    });
